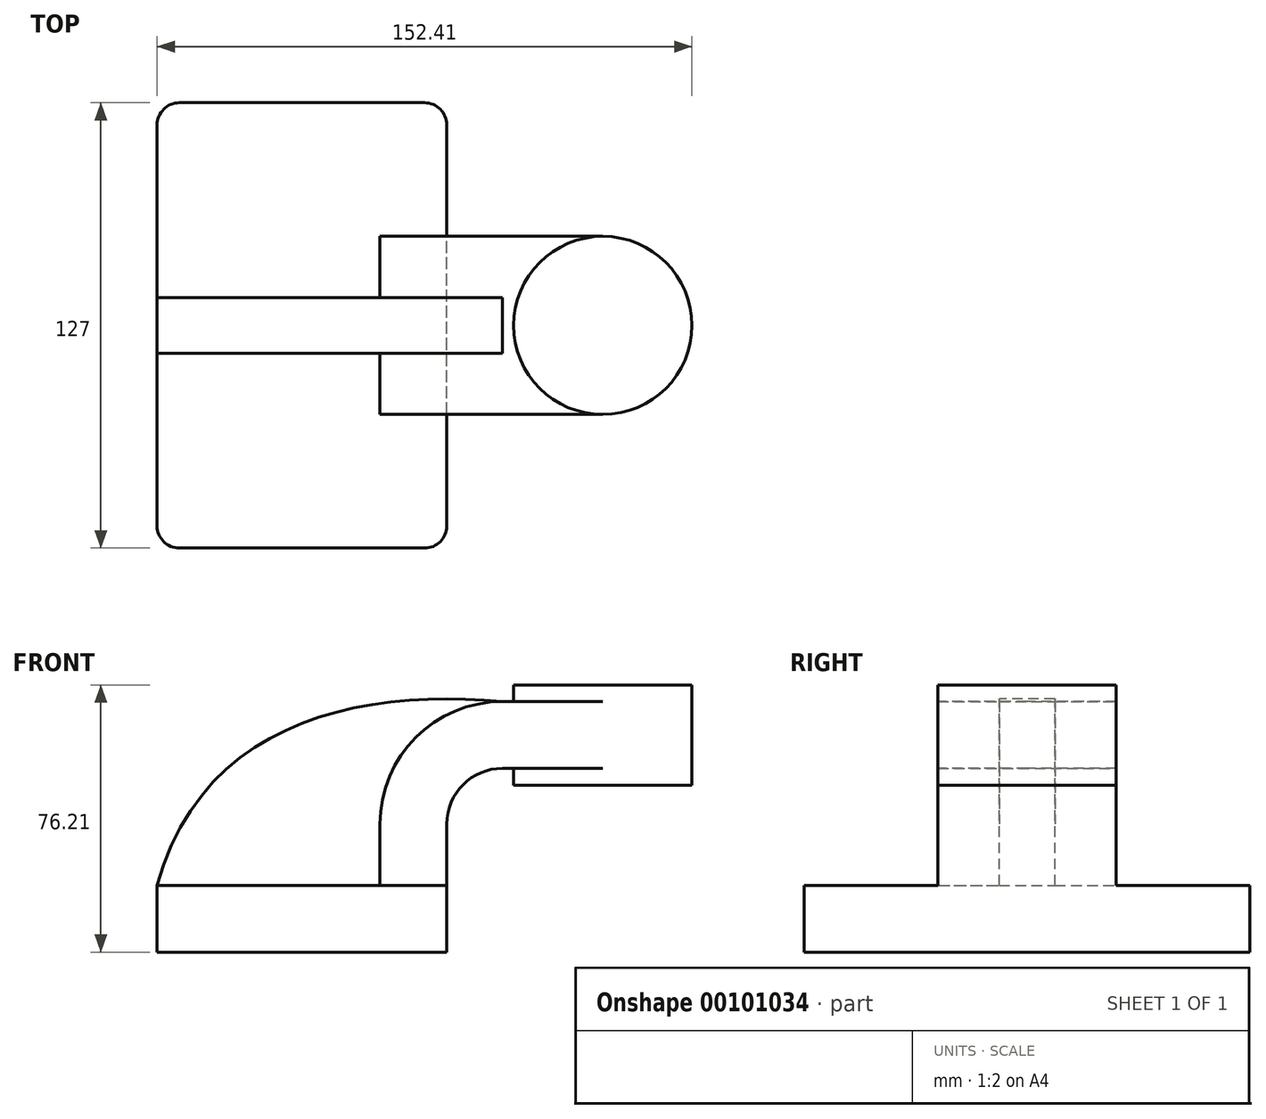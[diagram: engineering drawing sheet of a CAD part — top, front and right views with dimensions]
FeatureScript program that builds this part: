
annotation { "Feature Type Name" : "Feature", "Feature Type Description" : "" }
export const myFeature = defineFeature(function(context is Context, id is Id, definition is map)
    precondition{}
    {
        {
            var Q0;
            Q0=qCreatedBy(makeId("Front.planeOp"),FACE);
            var sketch = newSketch(context, id + "F0", { "sketchPlane" : qUnion([Q0])});
            skLineSegment(sketch, "E0.bottom", {"start": v(-41.27, -9.52) * mm, "end": v(41.28, -9.52) * mm});
            skLineSegment(sketch, "E0.top", {"start": v(-41.28, 9.53) * mm, "end": v(41.27, 9.53) * mm});
            skLineSegment(sketch, "E0.left", {"start": v(-41.27, -9.52) * mm, "end": v(-41.28, 9.53) * mm});
            skLineSegment(sketch, "E0.right", {"start": v(41.28, -9.52) * mm, "end": v(41.27, 9.53) * mm});
            skPoint(sketch, "E0.middle", {"position": v(0, 0) * mm});
            skLineSegment(sketch, "E1.bottom", {"start": v(60.33, 38.1) * mm, "end": v(111.13, 38.1) * mm});
            skLineSegment(sketch, "E1.top", {"start": v(60.33, 66.68) * mm, "end": v(111.13, 66.68) * mm});
            skLineSegment(sketch, "E1.left", {"start": v(60.33, 38.1) * mm, "end": v(60.33, 66.68) * mm});
            skLineSegment(sketch, "E1.right", {"start": v(111.13, 38.1) * mm, "end": v(111.13, 66.68) * mm});
            skPoint(sketch, "E1.middle", {"position": v(85.73, 52.39) * mm});
            skLineSegment(sketch, "E2", {"start": v(41.27, 9.53) * mm, "end": v(41.27, 27) * mm});
            skArc(sketch, "E3", {"start": v(57.15, 42.88) * mm, "mid": v(45.92, 38.23) * mm, "end": v(41.27, 27) * mm});
            skLineSegment(sketch, "E4", {"start": v(57.15, 42.88) * mm, "end": v(85.73, 42.88) * mm});
            skLineSegment(sketch, "E5.0", {"start": v(57.15, 61.93) * mm, "end": v(85.73, 61.93) * mm});
            skArc(sketch, "E5.1", {"start": v(57.15, 61.93) * mm, "mid": v(32.45, 51.7) * mm, "end": v(22.22, 27) * mm});
            skLineSegment(sketch, "E5.2", {"start": v(22.22, 9.53) * mm, "end": v(22.22, 27) * mm});
            skLineSegment(sketch, "E6", {"start": v(85.73, 38.1) * mm, "end": v(85.73, 66.68) * mm});
            skFitSpline(sketch, "E7", {"points": [v(-41.28, 9.53) * mm, v(57.15, 61.93) * mm], "startDerivative": vector(38.64, 140.83) * mm, "endDerivative": vector(120.85, -11.27) * mm});
            skSolve(sketch);
        }
        {
            var Q0;
            Q0=makeQuery(id+"F0.imprint","IMPRINT",FACE,{"disambiguationData":[TD([[makeQuery(id+"F0.imprint","IMPRINT",EDGE,{"derivedFrom":sQuery(id+"F0.wireOp",EDGE,"E0.bottom")}),1.0]])]});
            extrude(context, id + "F1", {"entities" : qUnion([Q0]), "endBound" : BoundingType.SYMMETRIC, "depth" : 127 * mm});
        }
        {
            var Q0;
            {var subQ1=sQuery(id+"F0.wireOp",EDGE,"E2");Q0=makeQuery(id+"F0.imprint","IMPRINT",FACE,{"disambiguationData":[TD([[makeQuery(id+"F0.imprint","IMPRINT",EDGE,{"derivedFrom":subQ1}),1.0]])]});}
            var Q1;
            {var subQ0=sQuery(id+"F0.wireOp",EDGE,"E4");var subQ1=sQuery(id+"F0.wireOp",EDGE,"E1.left");var subQ2=makeQuery(id+"F0.imprint","INTERSECT",VERTEX,{"derivedFrom":[subQ1,subQ0]});Q1=makeQuery(id+"F0.imprint","IMPRINT",FACE,{"disambiguationData":[TD([[makeQuery(id+"F0.imprint","IMPRINT",EDGE,{"disambiguationData":[TD([[subQ2,-1.0]])],"derivedFrom":subQ1}),-1.0]])]});}
            extrude(context, id + "F2", {"entities" : qUnion([Q0, Q1]), "operationType" : NewBodyOperationType.ADD, "endBound" : BoundingType.SYMMETRIC, "depth" : 50.8 * mm});
        }
        {
            var Q0;
            Q0=makeQuery(id+"F0.imprint","IMPRINT",FACE,{"disambiguationData":[TD([[makeQuery(id+"F0.imprint","IMPRINT",EDGE,{"derivedFrom":sQuery(id+"F0.wireOp",EDGE,"E5.1")}),-1.0]])]});
            extrude(context, id + "F3", {"entities" : qUnion([Q0]), "operationType" : NewBodyOperationType.ADD, "endBound" : BoundingType.SYMMETRIC, "depth" : 15.88 * mm});
        }
        {
            var Q0;
            {var subQ0=sQuery(id+"F0.wireOp",EDGE,"E1.right");Q0=makeQuery(id+"F0.imprint","IMPRINT",FACE,{"disambiguationData":[TD([[makeQuery(id+"F0.imprint","IMPRINT",EDGE,{"derivedFrom":subQ0}),1.0]])]});}
            var Q1;
            Q1=sQuery(id+"F0.wireOp",EDGE,"E6");
            revolve(context, id + "F4", {"operationType" : NewBodyOperationType.ADD, "entities" : qUnion([Q0]), "axis" : qUnion([Q1]), "revolveType" : RevolveType.FULL});
        }
        {
            var Q0;
            Q0=makeQuery(id+"F1.opExtrude","CAP_EDGE",EDGE,{"disambiguationData":[OSD([sQuery(id+"F0.wireOp",EDGE,"E0.left")])],"isStart":false});
            var Q1;
            Q1=makeQuery(id+"F1.opExtrude","CAP_EDGE",EDGE,{"disambiguationData":[OSD([sQuery(id+"F0.wireOp",EDGE,"E0.right")])],"isStart":false});
            var Q2;
            Q2=makeQuery(id+"F1.opExtrude","CAP_EDGE",EDGE,{"disambiguationData":[OSD([sQuery(id+"F0.wireOp",EDGE,"E0.right")])],"isStart":true});
            var Q3;
            Q3=makeQuery(id+"F1.opExtrude","CAP_EDGE",EDGE,{"disambiguationData":[OSD([sQuery(id+"F0.wireOp",EDGE,"E0.left")])],"isStart":true});
            fillet(context, id + "F5", {"entities" : qUnion([Q0, Q1, Q2, Q3]), "radius" : 6.35 * mm, "tangentPropagation" : true, "allowEdgeOverflow" : false});
        }
    });
